# Revit family: 306_H6_X_-SP2
name_source: partatom
category: Pipe Accessories
units: mm (PartAtom-declared; Revit-internal decimal feet)

## family parameters
Always vertical = Yes
Cut with Voids When Loaded = No
Part Type = Valve - Breaks Into
Round Connector Dimension = Use Diameter
Shared = No
Work Plane-Based = No

## types (3) — shared parameters
CAT0 = Yes
CenSd_NR_6 = 26 mm
Description = Globe valve, partial pressure relief, 2-way, Flange, PN 25
L2D_Min = 3048 mm
Manufacturer = Belimo
NR = 30 mm  [stored 0.0984252 ft]
QmdConnectorList = 301;D;302;D
magiPartTypeId = 306
magiProductFamilyId = H6*X*-SP2
zero-valued in all types: MC_Default_elevation

## per-type parameters (varying)
| type | C | C__ve | D | DD1 | DD2 | DR | FD | HH | HH1 | HH1__ve | HH2 | HH3 | HH4 | HH4__ve | HH5 | L2 | L2D | L4 | L42 | LL1 | LM | W2D |
| H6065X58-SP2 | 22 mm  [stored 0.0721785 ft] | -22 mm  [stored -0.0721785 ft] | 65 mm | 74 mm  [stored 0.242782 ft] | 130 mm | 46 mm | 185 mm | 78 mm | 16 mm | -16 mm | 47 mm | 62 mm  [stored 0.203412 ft] | 74 mm  [stored 0.242782 ft] | -74 mm  [stored -0.242782 ft] | 31 mm  [stored 0.101706 ft] | 145 mm | 290 mm | 73 mm | 51 mm  [stored 0.167323 ft] | 88 mm | 246 mm | 65 mm  [stored 0.213255 ft] |
| H6100X125-SP2 | 24 mm  [stored 0.0787402 ft] | -24 mm  [stored -0.0787402 ft] | 100 mm | 94 mm  [stored 0.308399 ft] | 165 mm | 59 mm | 235 mm | 95 mm  [stored 0.31168 ft] | 19 mm  [stored 0.062336 ft] | -19 mm  [stored -0.062336 ft] | 57 mm  [stored 0.187008 ft] | 76 mm  [stored 0.249344 ft] | 94 mm  [stored 0.308399 ft] | -94 mm  [stored -0.308399 ft] | 38 mm  [stored 0.124672 ft] | 175 mm | 350 mm | 88 mm | 65 mm  [stored 0.213255 ft] | 103 mm | 302 mm | 100 mm  [stored 0.328084 ft] |
| H6080X90-SP2 | 24 mm  [stored 0.0787402 ft] | -24 mm  [stored -0.0787402 ft] | 80 mm | 80 mm  [stored 0.262467 ft] | 140 mm | 50 mm  [stored 0.164042 ft] | 200 mm | 85 mm  [stored 0.278871 ft] | 17 mm  [stored 0.0557743 ft] | -17 mm  [stored -0.0557743 ft] | 51 mm  [stored 0.167323 ft] | 68 mm  [stored 0.223097 ft] | 80 mm  [stored 0.262467 ft] | -80 mm  [stored -0.262467 ft] | 34 mm  [stored 0.111549 ft] | 155 mm | 310 mm | 78 mm | 55 mm  [stored 0.180446 ft] | 93 mm  [stored 0.305118 ft] | 262 mm | 80 mm  [stored 0.262467 ft] |

note: column(s) folded — value = type name in every type: magiProductCode, magiProductId

note: [stored X ft] marks values corroborated as IEEE doubles in the binary element streams (Revit-internal decimal feet)

## geometry (parser evidence)
native form markers: Sweep x2
no freeform markers — native parametric forms only
